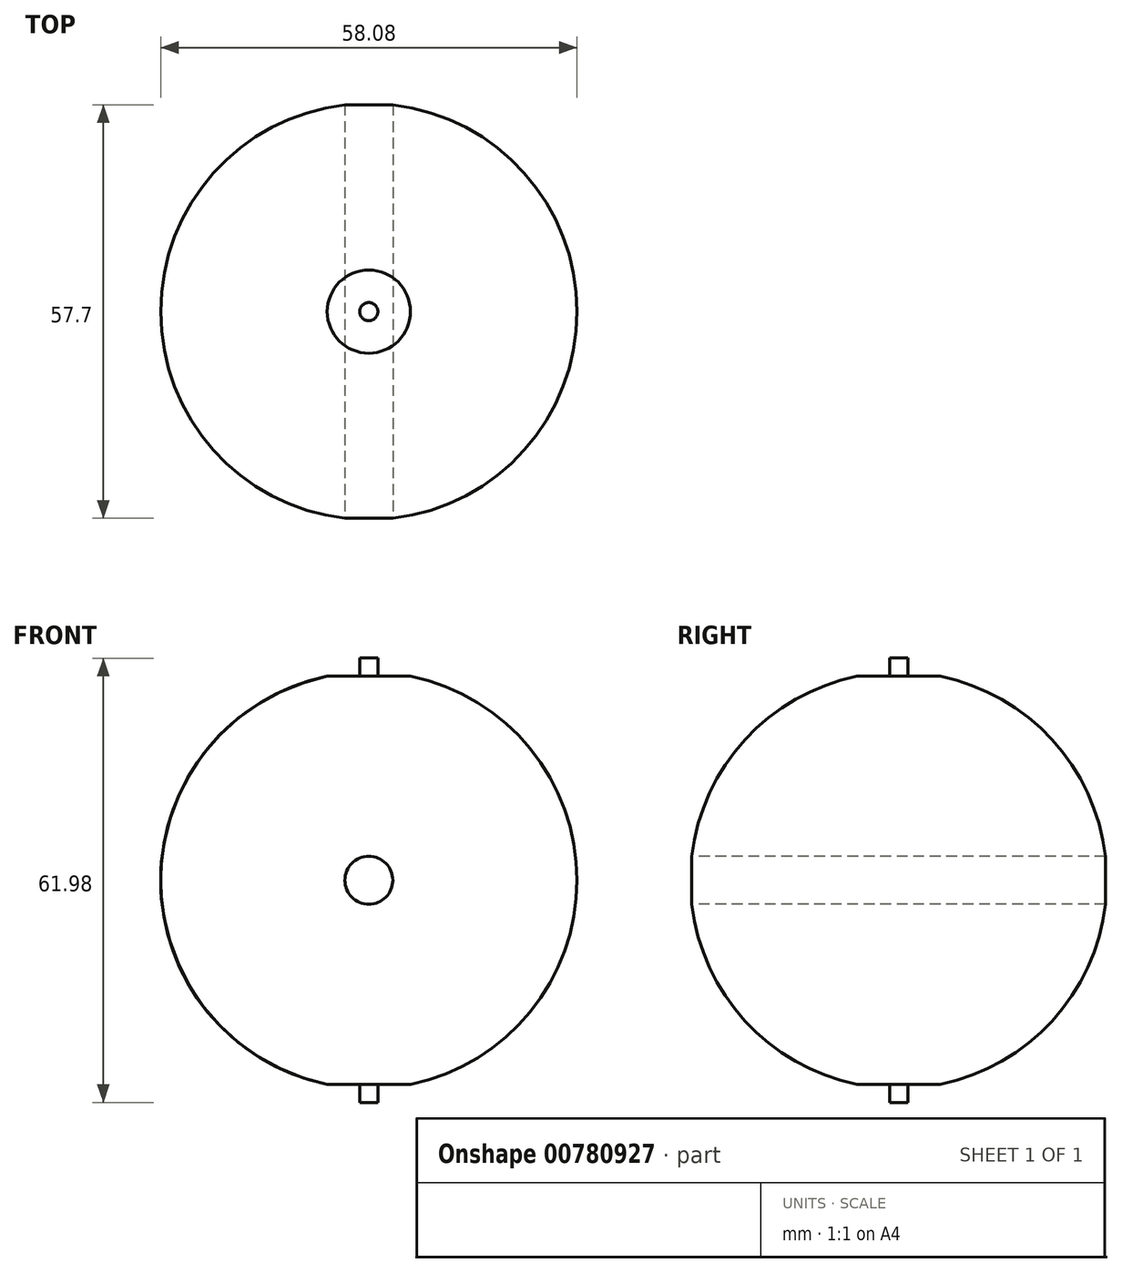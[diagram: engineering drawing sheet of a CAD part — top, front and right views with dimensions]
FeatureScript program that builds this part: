
annotation { "Feature Type Name" : "Feature", "Feature Type Description" : "" }
export const myFeature = defineFeature(function(context is Context, id is Id, definition is map)
    precondition{}
    {
        {
            var Q0;
            Q0=qCreatedBy(makeId("Front.planeOp"),FACE);
            var sketch = newSketch(context, id + "F0", { "sketchPlane" : qUnion([Q0])});
            skCircle(sketch, "E0", {"center": v(0, 0) * mm, "radius": 29.04 * mm});
            skLineSegment(sketch, "E1", {"start": v(0, 29.04) * mm, "end": v(0, -29.04) * mm});
            skSolve(sketch);
        }
        {
            var Q0;
            {var subQ0=sQuery(id+"F0.wireOp",EDGE,"E1");Q0=makeQuery(id+"F0.imprint","IMPRINT",FACE,{"disambiguationData":[TD([[makeQuery(id+"F0.imprint","IMPRINT",EDGE,{"derivedFrom":subQ0}),1.0]])]});}
            var Q1;
            Q1=sQuery(id+"F0.wireOp",EDGE,"E1");
            revolve(context, id + "F1", {"surfaceOperationType" : NewSurfaceOperationType.NEW, "entities" : qUnion([Q0]), "axis" : qUnion([Q1]), "revolveType" : RevolveType.FULL});
        }
        {
            var Q0;
            Q0=qCreatedBy(makeId("Right.planeOp"),FACE);
            var sketch = newSketch(context, id + "F2", { "sketchPlane" : qUnion([Q0])});
            skLineSegment(sketch, "E2", {"start": v(0, 28.45) * mm, "end": v(29.32, 28.45) * mm});
            skLineSegment(sketch, "E3", {"start": v(29.32, 28.45) * mm, "end": v(29.32, 34.25) * mm});
            skLineSegment(sketch, "E4", {"start": v(29.32, 34.25) * mm, "end": v(-33, 34.25) * mm});
            skLineSegment(sketch, "E5", {"start": v(-33, 34.25) * mm, "end": v(-33, 28.45) * mm});
            skLineSegment(sketch, "E6", {"start": v(-33, 28.45) * mm, "end": v(0, 28.45) * mm});
            skLineSegment(sketch, "E7", {"start": v(-32.84, -28.45) * mm, "end": v(-32.84, -37.7) * mm});
            skLineSegment(sketch, "E8", {"start": v(-32.84, -37.7) * mm, "end": v(29.32, -37.7) * mm});
            skLineSegment(sketch, "E9", {"start": v(29.32, -37.7) * mm, "end": v(29.32, -29.66) * mm});
            skLineSegment(sketch, "E10", {"start": v(-32.84, -28.45) * mm, "end": v(29.44, -28.45) * mm});
            skLineSegment(sketch, "E11", {"start": v(29.44, -28.45) * mm, "end": v(29.32, -29.66) * mm});
            skSolve(sketch);
        }
        {
            var Q0;
            Q0 = qSketchRegion(id + "F2", true);
            extrude(context, id + "F3", {"entities" : qUnion([Q0]), "operationType" : NewBodyOperationType.REMOVE, "endBound" : BoundingType.SYMMETRIC, "oppositeDirection" : true, "depth" : 25.4 * mm, "offsetDistance" : 25.4 * mm});
        }
        {
            var Q0;
            Q0=makeQuery(id+"F3.boolean.opBoolean","COPY",FACE,{"derivedFrom":makeQuery(id+"F3.opExtrude","SWEPT_FACE",FACE,{"disambiguationData":[OSD([sQuery(id+"F2.wireOp",EDGE,"E2"),sQuery(id+"F2.wireOp",EDGE,"E6")])]})});
            var sketch = newSketch(context, id + "F4", { "sketchPlane" : qUnion([Q0])});
            skCircle(sketch, "E12", {"center": v(0, 0) * mm, "radius": 1.27 * mm});
            skSolve(sketch);
        }
        {
            var Q0;
            Q0 = qSketchRegion(id + "F4", true);
            extrude(context, id + "F5", {"entities" : qUnion([Q0]), "operationType" : NewBodyOperationType.REMOVE, "oppositeDirection" : true, "depth" : 2.54 * mm, "offsetDistance" : 25.4 * mm});
        }
        {
            var Q0;
            Q0=makeQuery(id+"F3.boolean.opBoolean","COPY",FACE,{"derivedFrom":makeQuery(id+"F3.opExtrude","SWEPT_FACE",FACE,{"disambiguationData":[OSD([sQuery(id+"F2.wireOp",EDGE,"E10")])]})});
            var sketch = newSketch(context, id + "F6", { "sketchPlane" : qUnion([Q0])});
            skCircle(sketch, "E13", {"center": v(0, 0) * mm, "radius": 1.27 * mm});
            skSolve(sketch);
        }
        {
            var Q0;
            Q0 = qSketchRegion(id + "F6", true);
            extrude(context, id + "F7", {"entities" : qUnion([Q0]), "operationType" : NewBodyOperationType.REMOVE, "oppositeDirection" : true, "depth" : 2.54 * mm, "offsetDistance" : 25.4 * mm});
        }
        {
            var Q0;
            Q0=makeQuery(id+"F5.boolean.opBoolean","COPY",FACE,{"derivedFrom":makeQuery(id+"F5.opExtrude","CAP_FACE",FACE,{"disambiguationData":[OSD([sQuery(id+"F4.wireOp",EDGE,"E12")])],"isStart":false})});
            extrude(context, id + "F8", {"entities" : qUnion([Q0]), "operationType" : NewBodyOperationType.ADD, "depth" : 5.08 * mm, "offsetDistance" : 25.4 * mm});
        }
        {
            var Q0;
            Q0=makeQuery(id+"F7.boolean.opBoolean","COPY",FACE,{"derivedFrom":makeQuery(id+"F7.opExtrude","CAP_FACE",FACE,{"disambiguationData":[OSD([sQuery(id+"F6.wireOp",EDGE,"E13")])],"isStart":false})});
            extrude(context, id + "F9", {"entities" : qUnion([Q0]), "operationType" : NewBodyOperationType.ADD, "depth" : 5.08 * mm, "offsetDistance" : 25.4 * mm});
        }
        {
            var Q0;
            Q0=qCreatedBy(makeId("Front.planeOp"),FACE);
            var sketch = newSketch(context, id + "F10", { "sketchPlane" : qUnion([Q0])});
            skCircle(sketch, "E14", {"center": v(0, 0) * mm, "radius": 3.34 * mm});
            skSolve(sketch);
        }
        {
            var Q0;
            Q0 = qSketchRegion(id + "F10", true);
            extrude(context, id + "F11", {"entities" : qUnion([Q0]), "operationType" : NewBodyOperationType.REMOVE, "endBound" : BoundingType.SYMMETRIC, "oppositeDirection" : true, "depth" : 84.33 * mm, "offsetDistance" : 25.4 * mm});
        }
    });
